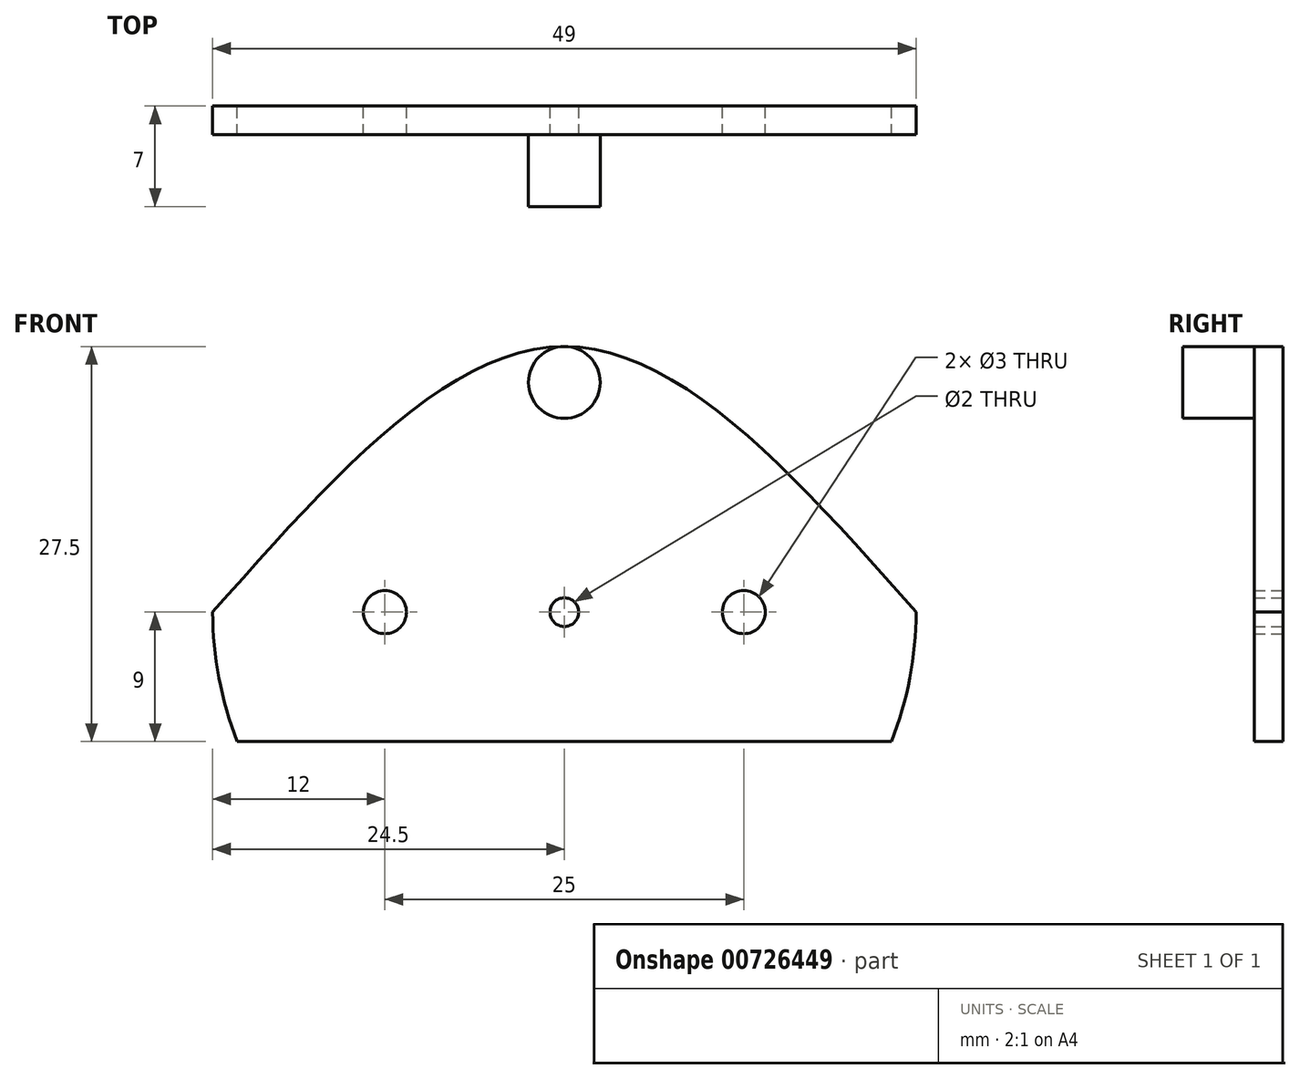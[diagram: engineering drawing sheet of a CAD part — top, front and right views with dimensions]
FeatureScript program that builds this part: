
annotation { "Feature Type Name" : "Feature", "Feature Type Description" : "" }
export const myFeature = defineFeature(function(context is Context, id is Id, definition is map)
    precondition{}
    {
        {
            var Q0;
            Q0=qCreatedBy(makeId("Front.planeOp"),FACE);
            var sketch = newSketch(context, id + "F0", { "sketchPlane" : qUnion([Q0])});
            skCircle(sketch, "E0", {"center": v(0, 0) * mm, "radius": 24.5 * mm});
            skCircle(sketch, "E1", {"center": v(-12.5, 0) * mm, "radius": 1.5 * mm});
            skCircle(sketch, "E2", {"center": v(12.5, 0) * mm, "radius": 1.5 * mm});
            skLineSegment(sketch, "E3", {"start": v(0, -24.5) * mm, "end": v(0, 0) * mm});
            skCircle(sketch, "E4", {"center": v(0, 0) * mm, "radius": 1 * mm});
            skLineSegment(sketch, "E5", {"start": v(-22.79, -9) * mm, "end": v(22.79, -9) * mm});
            skSolve(sketch);
        }
        {
            var Q0;
            Q0=makeQuery(id+"F0.imprint","IMPRINT",FACE,{"disambiguationData":[TD([[makeQuery(id+"F0.imprint","IMPRINT",EDGE,{"derivedFrom":sQuery(id+"F0.wireOp",EDGE,"E1")}),-1.0]])]});
            extrude(context, id + "F1", {"entities" : qUnion([Q0]), "depth" : 2 * mm, "offsetDistance" : 25 * mm});
        }
        {
            var Q0;
            Q0=makeQuery(id+"F1.opExtrude","CAP_FACE",FACE,{"disambiguationData":[OSD([sQuery(id+"F0.wireOp",EDGE,"E0"),sQuery(id+"F0.wireOp",EDGE,"E1"),sQuery(id+"F0.wireOp",EDGE,"E2"),sQuery(id+"F0.wireOp",EDGE,"E4"),sQuery(id+"F0.wireOp",EDGE,"E5")])],"isStart":false});
            var sketch = newSketch(context, id + "F2", { "sketchPlane" : qUnion([Q0])});
            skCircle(sketch, "E6", {"center": v(0, 16) * mm, "radius": 2.5 * mm});
            skSolve(sketch);
        }
        {
            var Q0;
            Q0=makeQuery(id+"F2.imprint","IMPRINT",FACE,{"disambiguationData":[TD([[makeQuery(id+"F2.imprint","IMPRINT",EDGE,{"derivedFrom":sQuery(id+"F2.wireOp",EDGE,"E6")}),1.0]])]});
            extrude(context, id + "F3", {"entities" : qUnion([Q0]), "operationType" : NewBodyOperationType.ADD, "depth" : 5 * mm, "offsetDistance" : 25 * mm});
        }
        {
            var Q0;
            Q0=makeQuery(id+"F1.opExtrude","CAP_FACE",FACE,{"disambiguationData":[OSD([sQuery(id+"F0.wireOp",EDGE,"E0"),sQuery(id+"F0.wireOp",EDGE,"E1"),sQuery(id+"F0.wireOp",EDGE,"E2"),sQuery(id+"F0.wireOp",EDGE,"E4"),sQuery(id+"F0.wireOp",EDGE,"E5")])],"isStart":false});
            var sketch = newSketch(context, id + "F4", { "sketchPlane" : qUnion([Q0])});
            skFitSpline(sketch, "E7", {"points": [v(-24.5, 0) * mm, v(0, 18.5) * mm, v(24.5, 0) * mm], "startDerivative": vector(49, 55.5) * mm, "endDerivative": vector(49, -55.5) * mm});
            skCircle(sketch, "E8", {"center": v(0, 0) * mm, "radius": 24.5 * mm});
            skSolve(sketch);
        }
        {
            var Q0;
            {var subQ0=sQuery(id+"F4.wireOp",EDGE,"E8");var subQ1=sQuery(id+"F4.wireOp",EDGE,"E7");var subQ2=makeQuery(id+"F4.imprint","INTERSECT",VERTEX,{"disambiguationData":[OD(0.0)],"derivedFrom":[subQ1,subQ0]});Q0=makeQuery(id+"F4.imprint","IMPRINT",FACE,{"disambiguationData":[TD([[makeQuery(id+"F4.imprint","IMPRINT",EDGE,{"disambiguationData":[TD([[subQ2,-1.0]])],"derivedFrom":subQ1}),1.0]])]});}
            extrude(context, id + "F5", {"entities" : qUnion([Q0]), "operationType" : NewBodyOperationType.REMOVE, "oppositeDirection" : true, "depth" : 25 * mm, "offsetDistance" : 25 * mm});
        }
    });
